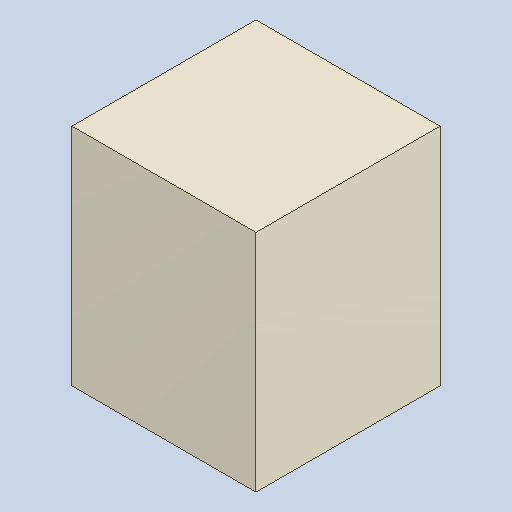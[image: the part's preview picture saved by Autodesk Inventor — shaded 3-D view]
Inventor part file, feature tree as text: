
AUTODESK INVENTOR PART (.ipt)
format: ipt  version: 2023.4 (Build 274418000, 418)  size: 82,944 bytes
history: native  units: mm
features: extrude x1
ambient origin geometry x8: Origin, YZ Plane, XZ Plane, XY Plane, X Axis, Y Axis, Z Axis, Center Point
bodies: Solid1 (feature_tree)
feature tree (1):
  extrude  "Extruded_14"  [1 undecoded]
note: 1 required parameter value undecoded (feature->parameter linkage not recoverable at this tier; creation-order binding heuristic only, values carry confidence <= 0.55)
